# Revit family: Domotics-DomesticRanges-GEWISS-CHORUS_COMMAND-PUSH-BUTTON_FAST_WIRING_2M
name_source: partatom
category: Apparecchi elettrici
revit_build: Autodesk Revit 2016 (Build: 20161004_0715(x64)
units: mm (PartAtom-declared; Revit-internal decimal feet)

## family parameters
Condiviso = Sì
Host = Superficie
Mantenere orientamento annotazione = Sì
Numero OmniClass = 23.80.50.11.14
Punto di calcolo locali = Sì
Quota connettore circolare = Usa diametro
Taglio con vuoti quando caricato = Sì
Tipo di parte = Normale
Titolo OmniClass = Switches

## types (9) — shared parameters
Breaking capacity = 1.25 In (200 position changes)
Breaking capacity: = 1.25 In (200 position changes)
Catalogue = DOMOTICS
Catalogue Range = CHORUS - DOMESTIC RANGE
Category = Push-button
Electrocod = 0130
GW10071F = No
GW10072F = No
GW10073F = Sì
Glow Wire Test = 850°C
IDF = 17749edc-ec97-4b90-83b3-a83e0ca27959
IDT = b7ac9d38-f869-40b4-9815-6d47a2b8e215
Immagine tipo = GW14173F.jpg
Insulation resistance = > 5 MOhm
L = 45 mm  [stored 0.147638 ft]
No. Chorus modules = 2
Produttore = GEWISS S.p.A.
Prolonged operation (no.of position changes) = 40.000 at In 250 V ac cosÃ˜=0,6
Prospetto di default = 1219 mm
Resistance at test voltage = 2000 V at 50 Hz for 1 minute
SEO = Push button
Standard = EN 60669-1
Standard; = EN 60669-1
Technical sheet = https://www.gewiss.com
Terminal grip on cable traction = > 50 N
Terminal tightening capacity = min. 0,75 - max. 2x4
Terminal tightening capacity flexible cables (mm2) = min. 0,75 - max. 2x4
Terminal tightening capacity rigid cables (mm2) = min. 0,5 - max. 2x2,5
Thermo-pressure with ball = 125
URL = https://www.gewiss.com
Version file RFA = 19.0
Voltage = 250 V ac
Voltage: = 250 V ac
Wiring terminals = Quick, with spring
finitura = titanio
sp = 5 mm  [stored 0.0164042 ft]
tipo = CHORUS PULSANTI 2M_BASE : GW14173F Pulsante 2M 1P NA 16A ititanio
tipologia = 2
w = 46 mm  [stored 0.150919 ft]

## per-type parameters (varying)
| type | Button key | Colour | Description: | Descrizione | EAN code | Modello | Type |
| GW10172F - Push-button 2M 1P NA 16A illuminable quick wiring White | With diffuser | White | 1P NO - 16A illuminable | PUSH-BUTTON, 2M 1P NO 16A ILL LOC R.W. W | 8011564258624 | GW10172F | Backlit |
| GW14172F - Push-button 2M 1P NA 16A illuminable quick wiring Titanium | With diffuser | Titanium | 1P NO - 16A illuminable | PUSH-BUTTON 2M 1P NO 16A ILL LOC R.W. T | 8011564266063 | GW14172F | Backlit |
| GW14173F - Push-button 2M 1P NA 16A illuminable quick wiring Titanium | With replaceable neutral lens | Titanium | 1P NO - 16A illuminable | PUSH-BUTTON 2M 1P NO 16A ILL SIG R.W. T | 8011564266087 | GW14173F | Indicator |
| GW14171F - Push-button 2M 1P NA 16A quick wiring Titanium | Neutral | Titanium | 1P NO - 16A | PUSH-BUTTON 2M 1P NO 16A R.W. TITANIUM | 8011564266049 | GW14171F | General |
| GW12173F - Push-button 2M 1P NA 16A illuminable quick wiring Black | With replaceable neutral lens | Black | 1P NO - 16A illuminable | PUSH-BUTTON, 2M 1P NO 16A ILL SIG R.W. B | 8011564269484 | GW12173F | Indicator |
| GW10171F - Push-button 2M 1P NA 16A quick wiring White | Neutral | White | 1P NO - 16A | PUSH-BUTTON, 2M 1P NO 16A R.W. WHITE | 8011564258600 | GW10171F | General |
| GW12171F - Push-button 2M 1P NA 16A quick wiring Black | Neutral | Black | 1P NO - 16A | PUSH-BUTTON, 2M 1P NO 16A R.WIRING BLACK | 8011564269446 | GW12171F | General |
| GW12172F - Push-button 2M 1P NA 16A illuminable quick wiring Black | With diffuser | Black | 1P NO - 16A illuminable | PUSH-BUTTON, 2M 1P NO 16A ILL LOC R.W. B | 8011564269460 | GW12172F | Backlit |
| GW10173F - Push-button 2M 1P NA 16A illuminable quick wiring White | With replaceable neutral lens | White | 1P NO - 16A illuminable | PUSH-BUTTON, 2M 1P NO 16A ILL SIG R.W. W | 8011564258648 | GW10173F | Indicator |

note: source unit labels omitted for Thermo-pressure with ball — the stored unit's dimension contradicts the parameter name (converter mislabeling)

note: [stored X ft] marks values corroborated as IEEE doubles in the binary element streams (Revit-internal decimal feet)

## geometry (parser evidence)
native form markers: Sweep x1
no freeform markers — native parametric forms only
